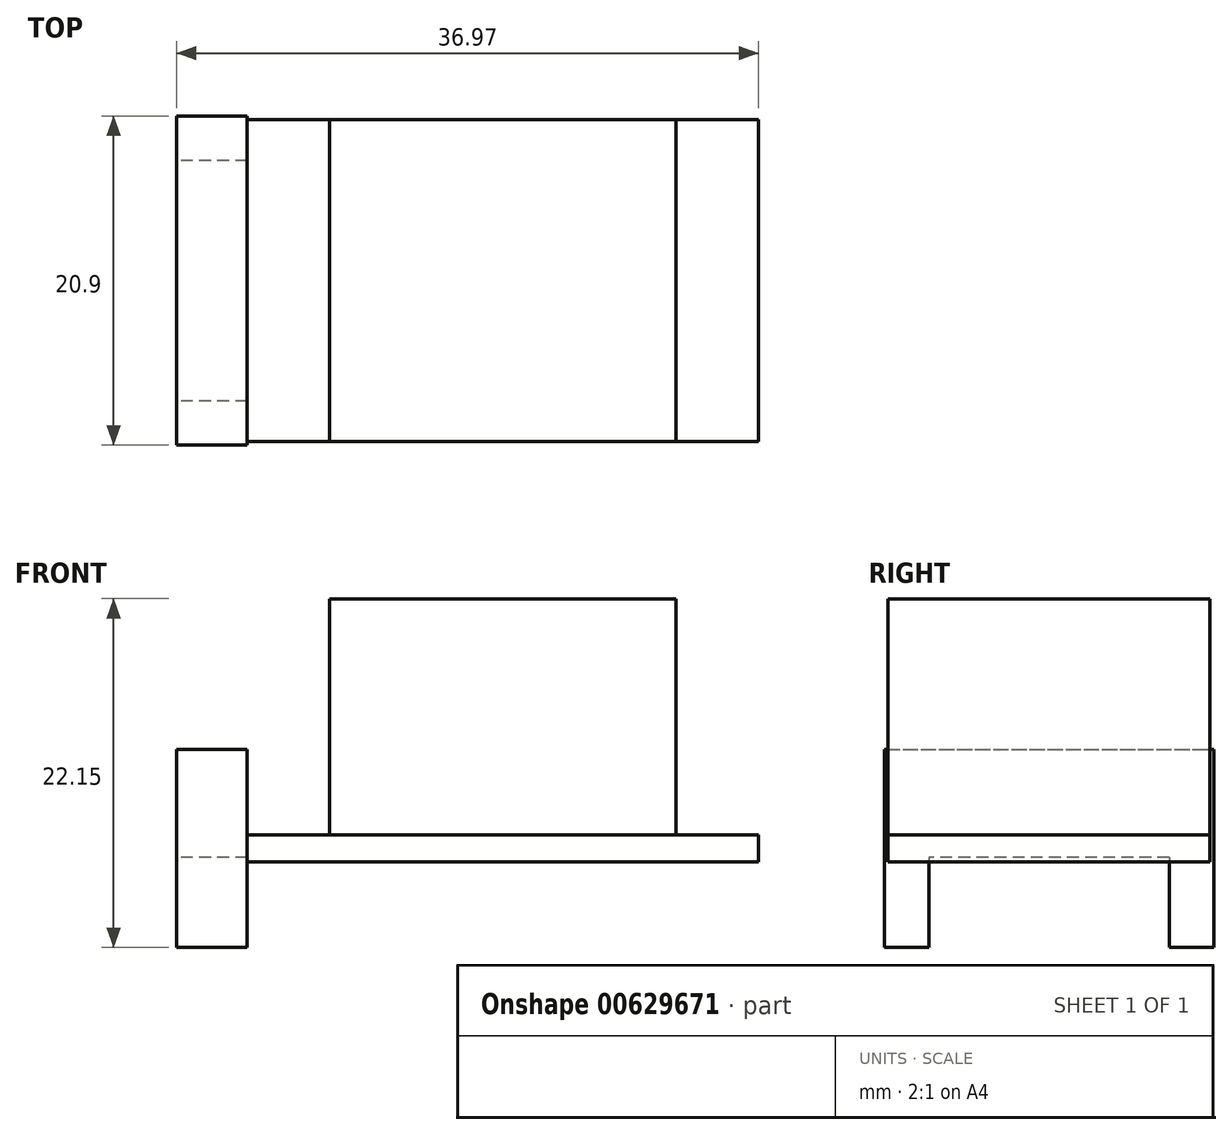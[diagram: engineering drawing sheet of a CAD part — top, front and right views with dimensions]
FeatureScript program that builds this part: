
annotation { "Feature Type Name" : "Feature", "Feature Type Description" : "" }
export const myFeature = defineFeature(function(context is Context, id is Id, definition is map)
    precondition{}
    {
        {
            var Q0;
            Q0=qCreatedBy(makeId("Top.planeOp"),FACE);
            var sketch = newSketch(context, id + "F0", { "sketchPlane" : qUnion([Q0])});
            skLineSegment(sketch, "E0.bottom", {"start": v(16.25, -10.22) * mm, "end": v(-16.25, -10.23) * mm});
            skLineSegment(sketch, "E0.top", {"start": v(16.25, 10.22) * mm, "end": v(-16.25, 10.22) * mm});
            skLineSegment(sketch, "E0.left", {"start": v(16.25, -10.22) * mm, "end": v(16.25, 10.23) * mm});
            skLineSegment(sketch, "E0.right", {"start": v(-16.25, -10.23) * mm, "end": v(-16.25, 10.22) * mm});
            skPoint(sketch, "E0.middle", {"position": v(0, 0) * mm});
            skSolve(sketch);
        }
        {
            var Q0;
            Q0=qSketchRegion(id+"F0",true);
            extrude(context, id + "F1", {"entities" : qUnion([Q0]), "endBound" : BoundingType.SYMMETRIC, "depth" : 1.71 * mm});
        }
        {
            var Q0;
            Q0=makeQuery(id+"F1.opExtrude","SWEPT_FACE",FACE,{"disambiguationData":[OSD([sQuery(id+"F0.wireOp",EDGE,"E0.right")])]});
            var sketch = newSketch(context, id + "F2", { "sketchPlane" : qUnion([Q0])});
            skLineSegment(sketch, "E1.bottom", {"start": v(10.45, -6.29) * mm, "end": v(-10.45, -6.29) * mm});
            skLineSegment(sketch, "E1.top", {"start": v(10.45, 6.29) * mm, "end": v(-10.45, 6.29) * mm});
            skLineSegment(sketch, "E1.left", {"start": v(10.45, -6.28) * mm, "end": v(10.45, 6.29) * mm});
            skLineSegment(sketch, "E1.right", {"start": v(-10.45, -6.29) * mm, "end": v(-10.45, 6.29) * mm});
            skPoint(sketch, "E1.middle", {"position": v(0, 0) * mm});
            skSolve(sketch);
        }
        {
            var Q0;
            Q0=qSketchRegion(id+"F2",true);
            extrude(context, id + "F3", {"entities" : qUnion([Q0]), "depth" : 4.48 * mm});
        }
        {
            var Q0;
            Q0=makeQuery(id+"F3.opExtrude","CAP_FACE",FACE,{"disambiguationData":[OSD([sQuery(id+"F2.wireOp",EDGE,"E1.bottom"),sQuery(id+"F2.wireOp",EDGE,"E1.top"),sQuery(id+"F2.wireOp",EDGE,"E1.left"),sQuery(id+"F2.wireOp",EDGE,"E1.right")])],"isStart":false});
            var sketch = newSketch(context, id + "F4", { "sketchPlane" : qUnion([Q0])});
            skLineSegment(sketch, "E2.bottom", {"start": v(7.64, -6.29) * mm, "end": v(-7.64, -6.29) * mm});
            skLineSegment(sketch, "E2.top", {"start": v(7.64, -0.56) * mm, "end": v(-7.64, -0.57) * mm});
            skLineSegment(sketch, "E2.left", {"start": v(7.64, -6.29) * mm, "end": v(7.64, -0.56) * mm});
            skLineSegment(sketch, "E2.right", {"start": v(-7.64, -6.29) * mm, "end": v(-7.64, -0.57) * mm});
            skPoint(sketch, "E2.middle", {"position": v(0, -3.43) * mm});
            skSolve(sketch);
        }
        {
            var Q0;
            Q0=makeQuery(id+"F4.imprint","IMPRINT",FACE,{"disambiguationData":[TD([[makeQuery(id+"F4.imprint","IMPRINT",EDGE,{"derivedFrom":sQuery(id+"F4.wireOp",EDGE,"E2.bottom")}),-1.0]])]});
            extrude(context, id + "F5", {"entities" : qUnion([Q0]), "operationType" : NewBodyOperationType.REMOVE, "endBound" : BoundingType.UP_TO_NEXT, "oppositeDirection" : true, "depth" : 25 * mm});
        }
        {
            var Q0;
            Q0=makeQuery(id+"F1.opExtrude","CAP_FACE",FACE,{"disambiguationData":[OSD([sQuery(id+"F0.wireOp",EDGE,"E0.bottom"),sQuery(id+"F0.wireOp",EDGE,"E0.top"),sQuery(id+"F0.wireOp",EDGE,"E0.left"),sQuery(id+"F0.wireOp",EDGE,"E0.right")])],"isStart":false});
            var sketch = newSketch(context, id + "F6", { "sketchPlane" : qUnion([Q0])});
            skLineSegment(sketch, "E3.bottom", {"start": v(11, -10.22) * mm, "end": v(-11, -10.22) * mm});
            skLineSegment(sketch, "E3.top", {"start": v(11, 10.22) * mm, "end": v(-11, 10.22) * mm});
            skLineSegment(sketch, "E3.left", {"start": v(11, -10.23) * mm, "end": v(11, 10.23) * mm});
            skLineSegment(sketch, "E3.right", {"start": v(-11, -10.23) * mm, "end": v(-11, 10.23) * mm});
            skPoint(sketch, "E3.middle", {"position": v(0, 0) * mm});
            skSolve(sketch);
        }
        {
            var Q0;
            Q0=qSketchRegion(id+"F6",true);
            extrude(context, id + "F7", {"entities" : qUnion([Q0]), "depth" : 15 * mm});
        }
    });
